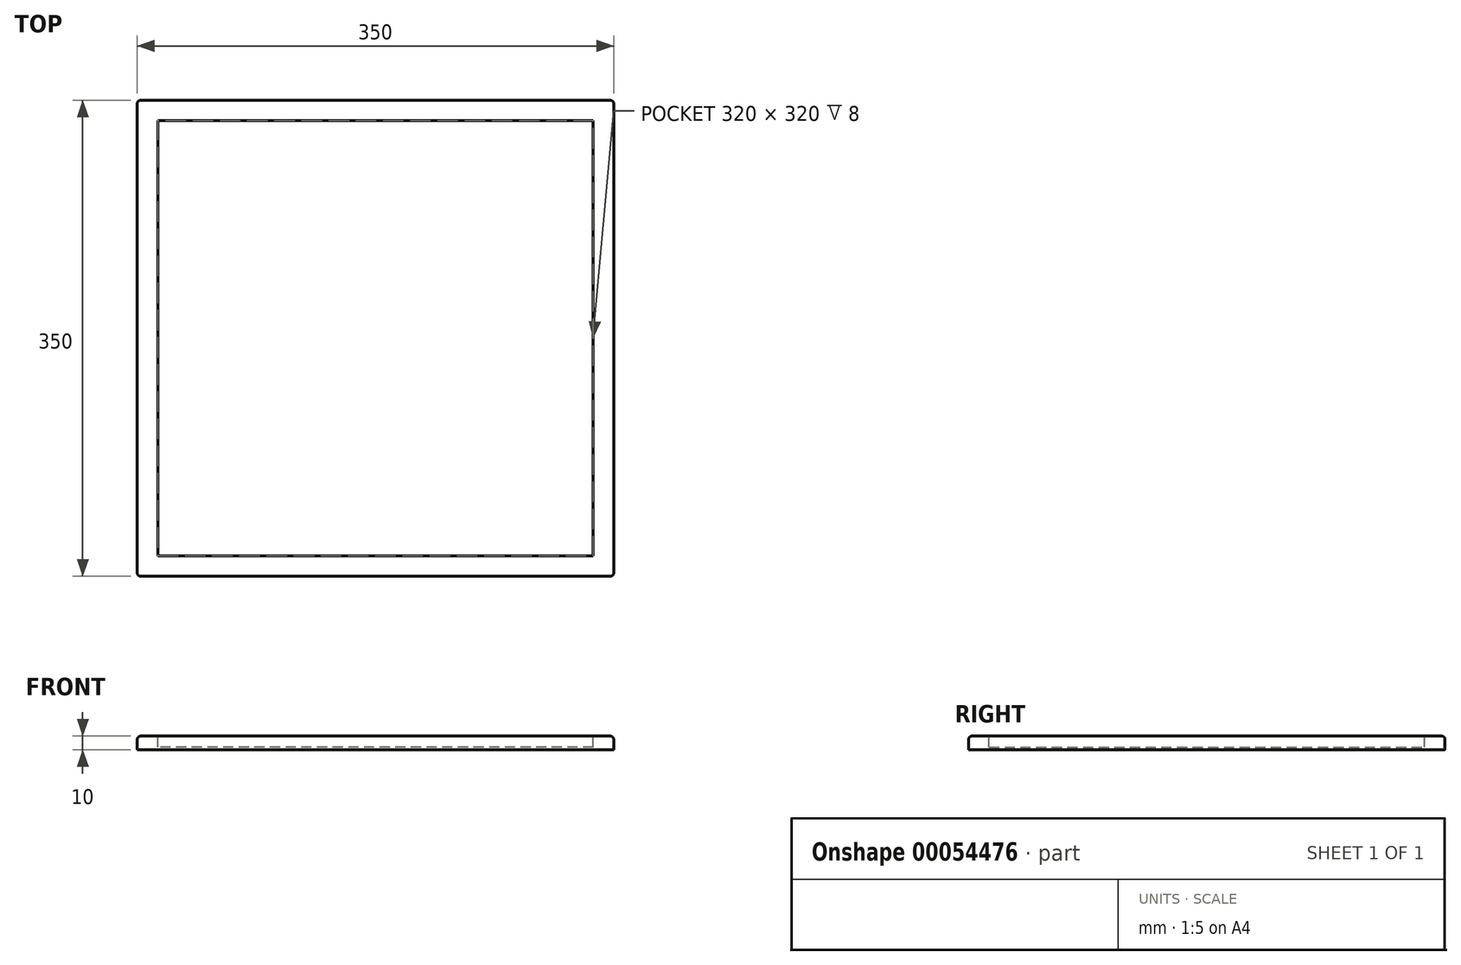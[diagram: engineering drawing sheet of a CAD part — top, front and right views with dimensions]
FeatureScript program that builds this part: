
annotation { "Feature Type Name" : "Feature", "Feature Type Description" : "" }
export const myFeature = defineFeature(function(context is Context, id is Id, definition is map)
    precondition{}
    {
        {
            var Q0;
            Q0=qCreatedBy(makeId("Top.planeOp"),FACE);
            var sketch = newSketch(context, id + "F0", { "sketchPlane" : qUnion([Q0])});
            skLineSegment(sketch, "E0.rect.bottom", {"start": v(175, -175) * mm, "end": v(-175, -175) * mm});
            skLineSegment(sketch, "E0.rect.top", {"start": v(175, 175) * mm, "end": v(-175, 175) * mm});
            skLineSegment(sketch, "E0.rect.left", {"start": v(175, -175) * mm, "end": v(175, 175) * mm});
            skLineSegment(sketch, "E0.rect.right", {"start": v(-175, -175) * mm, "end": v(-175, 175) * mm});
            skPoint(sketch, "E0.rect.middle", {"position": v(0, 0) * mm});
            skSolve(sketch);
        }
        {
            var Q0;
            Q0 = qSketchRegion(id + "F0", true);
            extrude(context, id + "F1", {"entities" : qUnion([Q0]), "depth" : 10 * mm});
        }
        {
            var Q0;
            Q0=makeQuery(id+"F1.opExtrude","CAP_FACE",FACE,{"disambiguationData":[OSD([sQuery(id+"F0.wireOp",EDGE,"E0.rect.bottom"),sQuery(id+"F0.wireOp",EDGE,"E0.rect.top"),sQuery(id+"F0.wireOp",EDGE,"E0.rect.left"),sQuery(id+"F0.wireOp",EDGE,"E0.rect.right")])],"isStart":false});
            var sketch = newSketch(context, id + "F2", { "sketchPlane" : qUnion([Q0])});
            skLineSegment(sketch, "E1.0", {"start": v(160, 160) * mm, "end": v(-160, 160) * mm});
            skLineSegment(sketch, "E1.1", {"start": v(160, -160) * mm, "end": v(160, 160) * mm});
            skLineSegment(sketch, "E1.2", {"start": v(160, -160) * mm, "end": v(-160, -160) * mm});
            skLineSegment(sketch, "E1.3", {"start": v(-160, -160) * mm, "end": v(-160, 160) * mm});
            skSolve(sketch);
        }
        {
            var Q0;
            Q0=makeQuery(id+"F2.imprint","IMPRINT",FACE,{"disambiguationData":[TD([[makeQuery(id+"F2.imprint","IMPRINT",EDGE,{"derivedFrom":sQuery(id+"F2.wireOp",EDGE,"E1.0")}),1.0]])]});
            extrude(context, id + "F3", {"entities" : qUnion([Q0]), "operationType" : NewBodyOperationType.REMOVE, "oppositeDirection" : true, "depth" : 8 * mm});
        }
        {
            var Q0;
            Q0=makeQuery(id+"F1.opExtrude","SWEPT_EDGE",EDGE,{"disambiguationData":[OSD([sQuery(id+"F0.wireOp",EDGE,"E0.rect.bottom"),sQuery(id+"F0.wireOp",EDGE,"E0.rect.left")])]});
            var Q1;
            Q1=makeQuery(id+"F1.opExtrude","CAP_EDGE",EDGE,{"disambiguationData":[OSD([sQuery(id+"F0.wireOp",EDGE,"E0.rect.left")])],"isStart":false});
            var Q2;
            Q2=makeQuery(id+"F1.opExtrude","CAP_EDGE",EDGE,{"disambiguationData":[OSD([sQuery(id+"F0.wireOp",EDGE,"E0.rect.bottom")])],"isStart":false});
            var Q3;
            Q3=makeQuery(id+"F1.opExtrude","SWEPT_EDGE",EDGE,{"disambiguationData":[OSD([sQuery(id+"F0.wireOp",EDGE,"E0.rect.bottom"),sQuery(id+"F0.wireOp",EDGE,"E0.rect.right")])]});
            var Q4;
            Q4=makeQuery(id+"F1.opExtrude","CAP_EDGE",EDGE,{"disambiguationData":[OSD([sQuery(id+"F0.wireOp",EDGE,"E0.rect.right")])],"isStart":false});
            var Q5;
            Q5=makeQuery(id+"F1.opExtrude","CAP_EDGE",EDGE,{"disambiguationData":[OSD([sQuery(id+"F0.wireOp",EDGE,"E0.rect.top")])],"isStart":false});
            var Q6;
            Q6=makeQuery(id+"F1.opExtrude","SWEPT_EDGE",EDGE,{"disambiguationData":[OSD([sQuery(id+"F0.wireOp",EDGE,"E0.rect.top"),sQuery(id+"F0.wireOp",EDGE,"E0.rect.right")])]});
            var Q7;
            Q7=makeQuery(id+"F1.opExtrude","SWEPT_EDGE",EDGE,{"disambiguationData":[OSD([sQuery(id+"F0.wireOp",EDGE,"E0.rect.top"),sQuery(id+"F0.wireOp",EDGE,"E0.rect.left")])]});
            fillet(context, id + "F4", {"entities" : qUnion([Q0, Q1, Q2, Q3, Q4, Q5, Q6, Q7]), "radius" : 2.5 * mm, "tangentPropagation" : true, "allowEdgeOverflow" : false});
        }
    });
